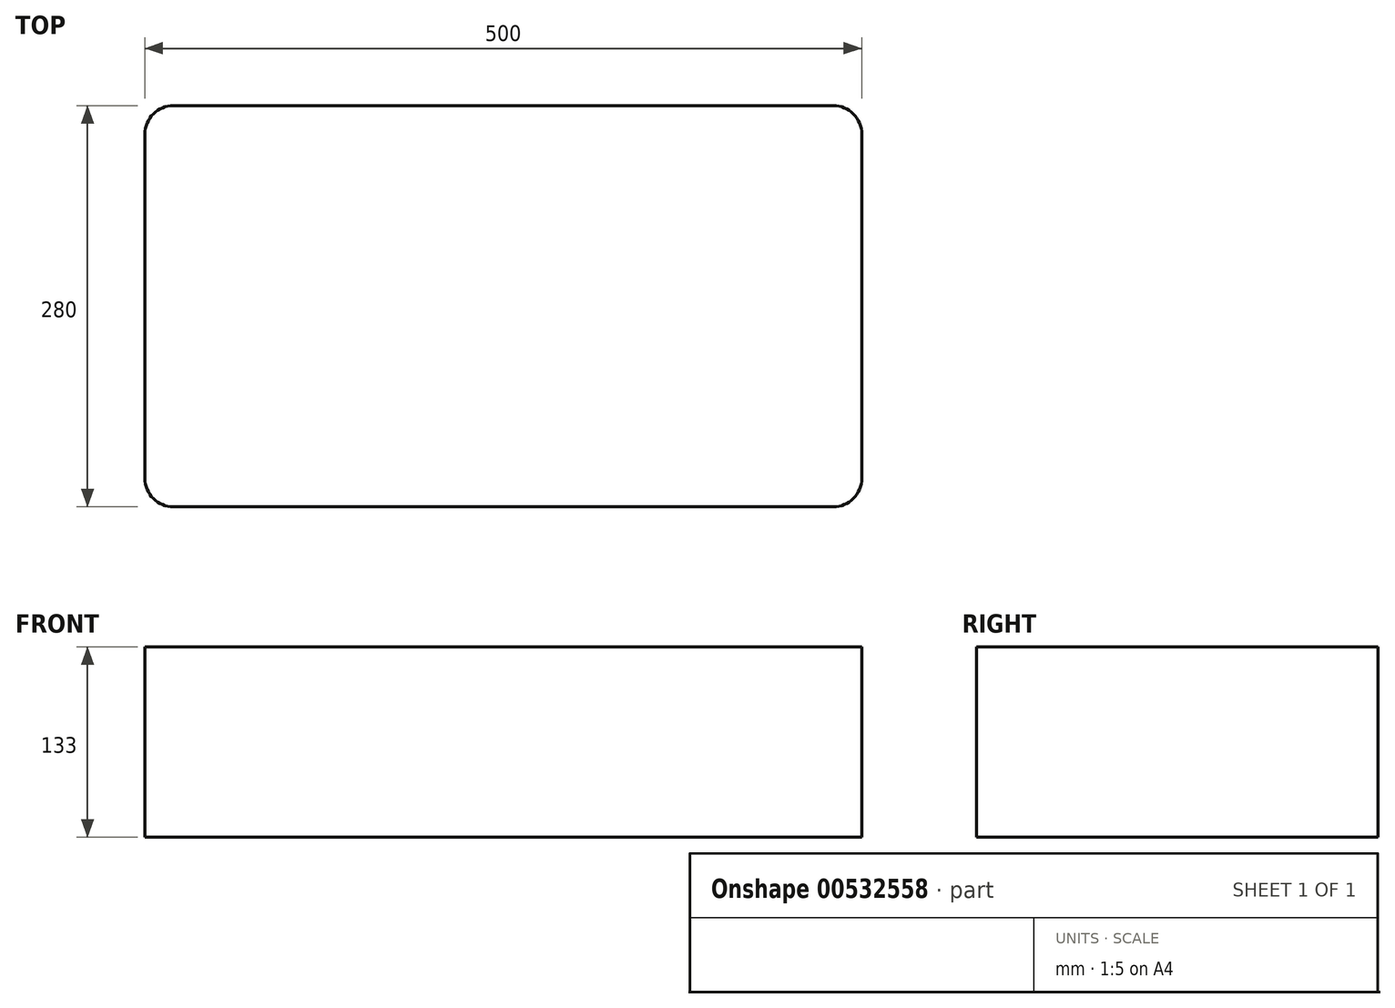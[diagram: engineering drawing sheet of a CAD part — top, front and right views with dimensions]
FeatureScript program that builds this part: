
annotation { "Feature Type Name" : "Feature", "Feature Type Description" : "" }
export const myFeature = defineFeature(function(context is Context, id is Id, definition is map)
    precondition{}
    {
        {
            var Q0;
            Q0=qCreatedBy(makeId("Top.planeOp"),FACE);
            var sketch = newSketch(context, id + "F0", { "sketchPlane" : qUnion([Q0])});
            skLineSegment(sketch, "E0.bottom", {"start": v(-230, 140) * mm, "end": v(230, 140) * mm});
            skLineSegment(sketch, "E0.top", {"start": v(-230, -140) * mm, "end": v(230, -140) * mm});
            skLineSegment(sketch, "E0.left", {"start": v(-250, 120) * mm, "end": v(-250, -120) * mm});
            skLineSegment(sketch, "E0.right", {"start": v(250, 120) * mm, "end": v(250, -120) * mm});
            skPoint(sketch, "E0.middle", {"position": v(0, 0) * mm});
            skPoint(sketch, "E1.visualSharp", {"position": v(-250, 140) * mm});
            skArc(sketch, "E1.filletArc", {"start": v(-230, 140) * mm, "mid": v(-244.14, 134.14) * mm, "end": v(-250, 120) * mm});
            skPoint(sketch, "E2.visualSharp", {"position": v(-250, -140) * mm});
            skArc(sketch, "E2.filletArc", {"start": v(-250, -120) * mm, "mid": v(-244.14, -134.14) * mm, "end": v(-230, -140) * mm});
            skPoint(sketch, "E3.visualSharp", {"position": v(250, -140) * mm});
            skArc(sketch, "E3.filletArc", {"start": v(230, -140) * mm, "mid": v(244.14, -134.14) * mm, "end": v(250, -120) * mm});
            skPoint(sketch, "E4.visualSharp", {"position": v(250, 140) * mm});
            skArc(sketch, "E4.filletArc", {"start": v(250, 120) * mm, "mid": v(244.14, 134.14) * mm, "end": v(230, 140) * mm});
            skSolve(sketch);
        }
        {
            var Q0;
            Q0 = qSketchRegion(id + "F0", true);
            extrude(context, id + "F1", {"entities" : qUnion([Q0]), "depth" : 133 * mm, "offsetDistance" : 25 * mm});
        }
    });
